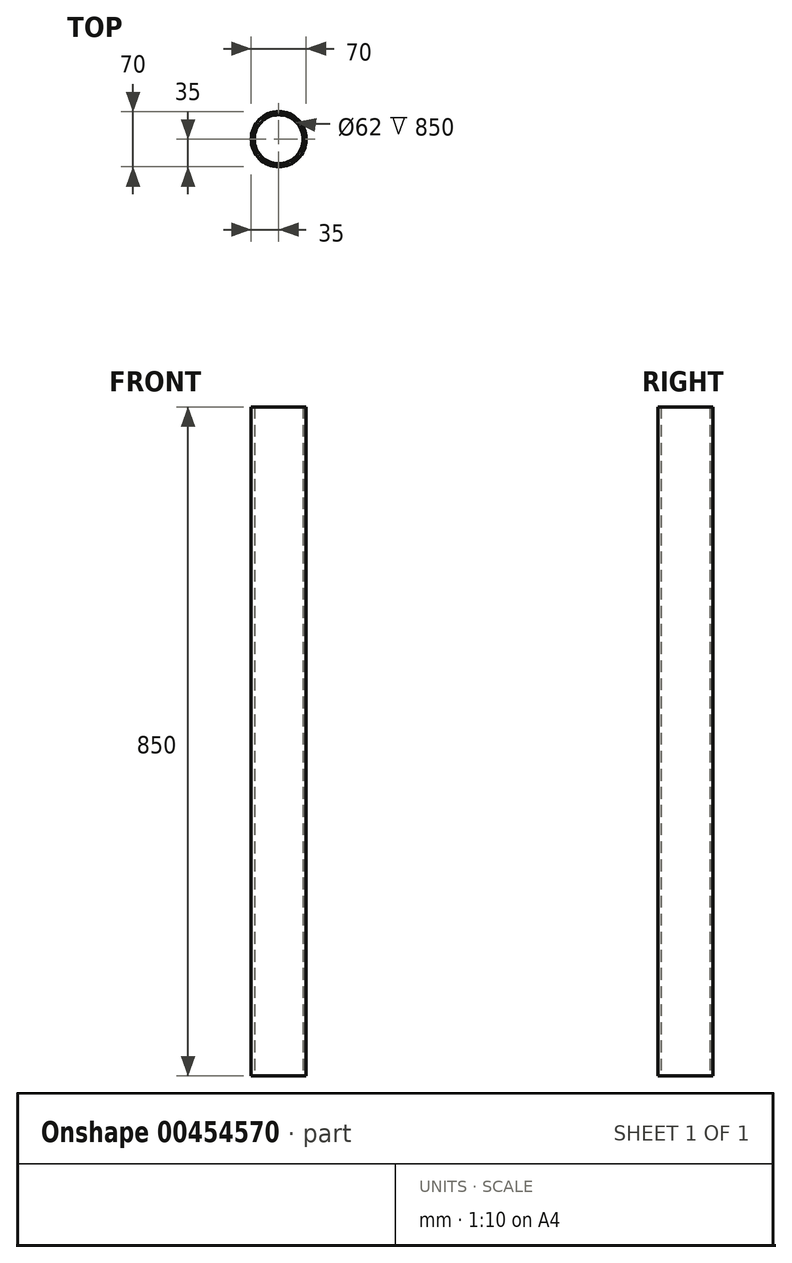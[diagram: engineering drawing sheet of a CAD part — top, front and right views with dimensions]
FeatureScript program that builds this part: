
annotation { "Feature Type Name" : "Feature", "Feature Type Description" : "" }
export const myFeature = defineFeature(function(context is Context, id is Id, definition is map)
    precondition{}
    {
        {
            var Q0;
            Q0=qCreatedBy(makeId("Front.planeOp"),FACE);
            var sketch = newSketch(context, id + "F0", { "sketchPlane" : qUnion([Q0])});
            skLineSegment(sketch, "E0", {"start": v(0, 0) * mm, "end": v(0, 35.16) * mm, "construction": true});
            skLineSegment(sketch, "E1", {"start": v(31, 0) * mm, "end": v(35, 0) * mm});
            skLineSegment(sketch, "E2", {"start": v(35, 0) * mm, "end": v(35, 850) * mm});
            skLineSegment(sketch, "E3", {"start": v(35, 850) * mm, "end": v(31, 850) * mm});
            skLineSegment(sketch, "E4", {"start": v(31, 850) * mm, "end": v(31, 0) * mm});
            skSolve(sketch);
        }
        {
            var Q0;
            Q0 = qSketchRegion(id + "F0", true);
            var Q1;
            Q1=sQuery(id+"F0.wireOp",EDGE,"E0");
            revolve(context, id + "F1", {"entities" : qUnion([Q0]), "axis" : qUnion([Q1]), "revolveType" : RevolveType.FULL});
        }
    });
